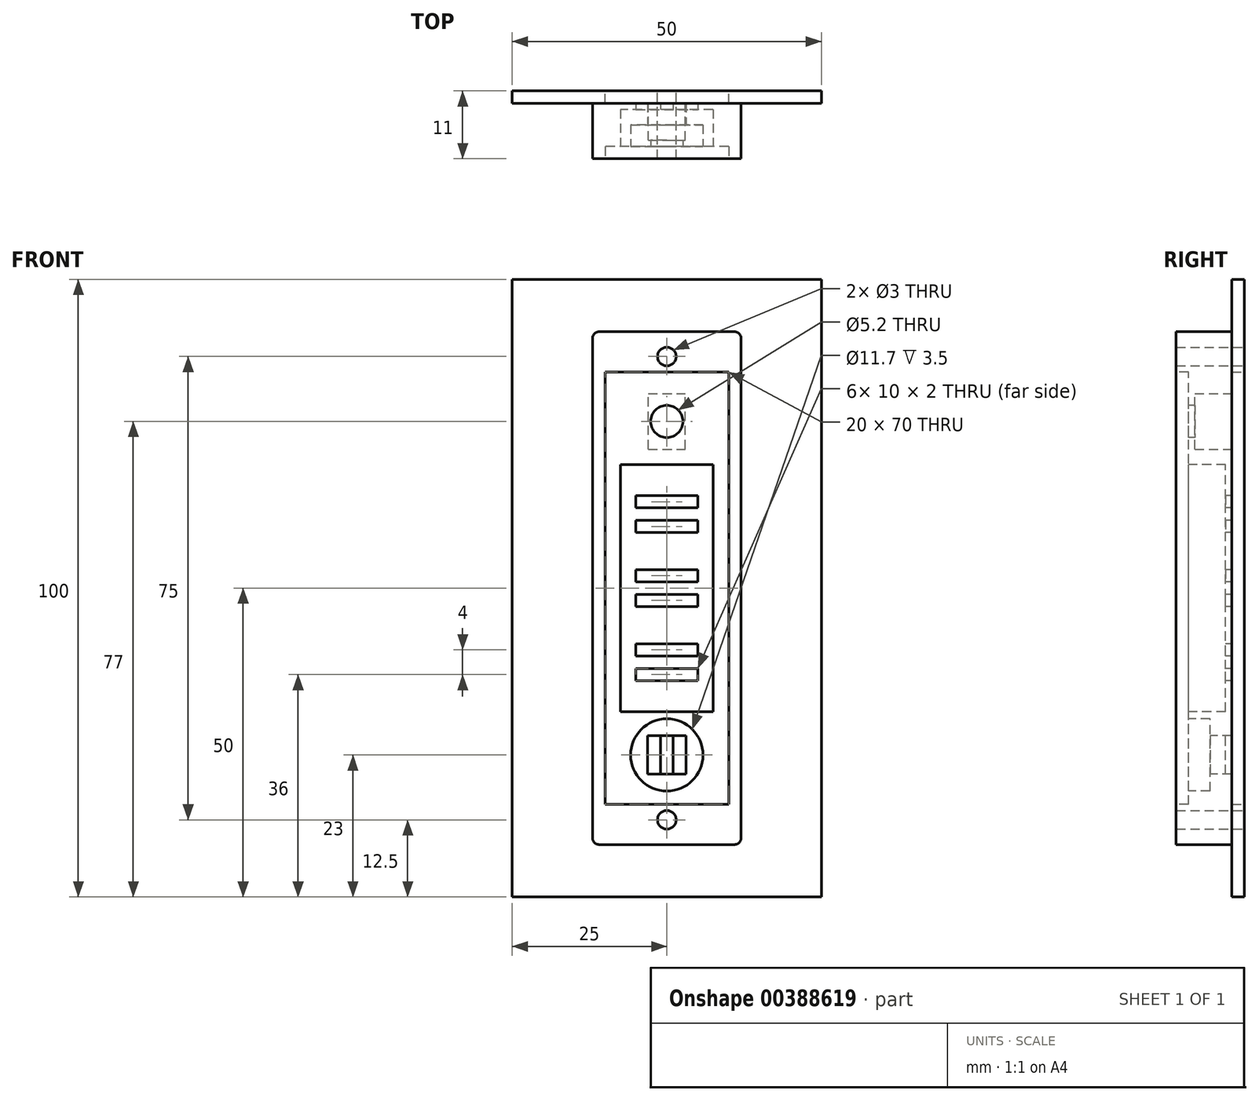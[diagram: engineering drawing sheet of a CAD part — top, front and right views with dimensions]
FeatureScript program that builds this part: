
annotation { "Feature Type Name" : "Feature", "Feature Type Description" : "" }
export const myFeature = defineFeature(function(context is Context, id is Id, definition is map)
    precondition{}
    {
        {
            var Q0;
            Q0=qCreatedBy(makeId("Front.planeOp"),FACE);
            var sketch = newSketch(context, id + "F0", { "sketchPlane" : qUnion([Q0])});
            skLineSegment(sketch, "E0.bottom", {"start": v(25, -50) * mm, "end": v(-25, -50) * mm});
            skLineSegment(sketch, "E0.top", {"start": v(25, 50) * mm, "end": v(-25, 50) * mm});
            skLineSegment(sketch, "E0.left", {"start": v(25, -50) * mm, "end": v(25, 50) * mm});
            skLineSegment(sketch, "E0.right", {"start": v(-25, -50) * mm, "end": v(-25, 50) * mm});
            skPoint(sketch, "E0.middle", {"position": v(0, 0) * mm});
            skLineSegment(sketch, "E1.bottom", {"start": v(10, -35) * mm, "end": v(-10, -35) * mm});
            skLineSegment(sketch, "E1.top", {"start": v(10, 35) * mm, "end": v(-10, 35) * mm});
            skLineSegment(sketch, "E1.left", {"start": v(10, -35) * mm, "end": v(10, 35) * mm});
            skLineSegment(sketch, "E1.right", {"start": v(-10, -35) * mm, "end": v(-10, 35) * mm});
            skCircle(sketch, "E2", {"center": v(0, 37.5) * mm, "radius": 1.5 * mm});
            skCircle(sketch, "E3", {"center": v(0, -37.5) * mm, "radius": 1.5 * mm});
            skSolve(sketch);
        }
        {
            var Q0;
            Q0 = qSketchRegion(id + "F0", true);
            extrude(context, id + "F1", {"entities" : qUnion([Q0]), "depth" : 2 * mm});
        }
        {
            var Q0;
            Q0=makeQuery(id+"F1.opExtrude","CAP_FACE",FACE,{"disambiguationData":[OSD([sQuery(id+"F0.wireOp",EDGE,"E0.bottom"),sQuery(id+"F0.wireOp",EDGE,"E0.top"),sQuery(id+"F0.wireOp",EDGE,"E0.left"),sQuery(id+"F0.wireOp",EDGE,"E0.right"),sQuery(id+"F0.wireOp",EDGE,"E1.bottom"),sQuery(id+"F0.wireOp",EDGE,"E1.top"),sQuery(id+"F0.wireOp",EDGE,"E1.left"),sQuery(id+"F0.wireOp",EDGE,"E1.right"),sQuery(id+"F0.wireOp",EDGE,"E2"),sQuery(id+"F0.wireOp",EDGE,"E3")])],"isStart":false});
            var sketch = newSketch(context, id + "F2", { "sketchPlane" : qUnion([Q0])});
            skLineSegment(sketch, "E4.bottom", {"start": v(12, -41.5) * mm, "end": v(-12, -41.5) * mm});
            skLineSegment(sketch, "E4.top", {"start": v(12, 41.5) * mm, "end": v(-12, 41.5) * mm});
            skLineSegment(sketch, "E4.left", {"start": v(12, -41.5) * mm, "end": v(12, 41.5) * mm});
            skLineSegment(sketch, "E4.right", {"start": v(-12, -41.5) * mm, "end": v(-12, 41.5) * mm});
            skPoint(sketch, "E4.middle", {"position": v(0, 0) * mm});
            skCircle(sketch, "E5", {"center": v(0, 37.5) * mm, "radius": 1.5 * mm});
            skCircle(sketch, "E6", {"center": v(0, -37.5) * mm, "radius": 1.5 * mm});
            skSolve(sketch);
        }
        {
            var Q0;
            Q0 = qSketchRegion(id + "F2", true);
            extrude(context, id + "F3", {"entities" : qUnion([Q0]), "depth" : 9 * mm});
        }
        {
            var Q0;
            Q0=makeQuery(id+"F3.opExtrude","CAP_FACE",FACE,{"disambiguationData":[OSD([sQuery(id+"F2.wireOp",EDGE,"E4.bottom"),sQuery(id+"F2.wireOp",EDGE,"E4.top"),sQuery(id+"F2.wireOp",EDGE,"E4.left"),sQuery(id+"F2.wireOp",EDGE,"E4.right")])],"isStart":false});
            var sketch = newSketch(context, id + "F4", { "sketchPlane" : qUnion([Q0])});
            skLineSegment(sketch, "E7.bottom", {"start": v(10, -35) * mm, "end": v(-10, -35) * mm});
            skLineSegment(sketch, "E7.top", {"start": v(10, 35) * mm, "end": v(-10, 35) * mm});
            skLineSegment(sketch, "E7.left", {"start": v(10, -35) * mm, "end": v(10, 35) * mm});
            skLineSegment(sketch, "E7.right", {"start": v(-10, -35) * mm, "end": v(-10, 35) * mm});
            skPoint(sketch, "E7.middle", {"position": v(0, 0) * mm});
            skSolve(sketch);
        }
        {
            var Q0;
            Q0 = qSketchRegion(id + "F4", true);
            extrude(context, id + "F5", {"entities" : qUnion([Q0]), "operationType" : NewBodyOperationType.REMOVE, "oppositeDirection" : true, "depth" : 14 * mm});
        }
        {
            var Q0;
            Q0=makeQuery(id+"F1.opExtrude","CAP_FACE",FACE,{"disambiguationData":[OSD([sQuery(id+"F0.wireOp",EDGE,"E0.bottom"),sQuery(id+"F0.wireOp",EDGE,"E0.top"),sQuery(id+"F0.wireOp",EDGE,"E0.left"),sQuery(id+"F0.wireOp",EDGE,"E0.right"),sQuery(id+"F0.wireOp",EDGE,"E1.bottom"),sQuery(id+"F0.wireOp",EDGE,"E1.top"),sQuery(id+"F0.wireOp",EDGE,"E1.left"),sQuery(id+"F0.wireOp",EDGE,"E1.right"),sQuery(id+"F0.wireOp",EDGE,"E2"),sQuery(id+"F0.wireOp",EDGE,"E3")])],"isStart":false});
            cPlane(context, id + "F6", {"entities" : qUnion([Q0]), "cplaneType" : CPlaneType.OFFSET, "offset" : 0 * mm, "width" : 150 * mm, "height" : 150 * mm});
        }
        {
            var Q0;
            Q0=qCreatedBy(id+"F6.planeOp",FACE);
            var sketch = newSketch(context, id + "F7", { "sketchPlane" : qUnion([Q0])});
            skLineSegment(sketch, "E8.bottom", {"start": v(10, -35) * mm, "end": v(-10, -35) * mm});
            skLineSegment(sketch, "E8.top", {"start": v(10, 35) * mm, "end": v(-10, 35) * mm});
            skLineSegment(sketch, "E8.left", {"start": v(10, -35) * mm, "end": v(10, 35) * mm});
            skLineSegment(sketch, "E8.right", {"start": v(-10, -35) * mm, "end": v(-10, 35) * mm});
            skPoint(sketch, "E8.middle", {"position": v(0, 0) * mm});
            skSolve(sketch);
        }
        {
            var Q0;
            Q0 = qSketchRegion(id + "F7", true);
            extrude(context, id + "F8", {"entities" : qUnion([Q0]), "operationType" : NewBodyOperationType.ADD, "depth" : 7 * mm});
        }
        {
            var Q0;
            Q0=makeQuery(id+"F8.opExtrude","CAP_FACE",FACE,{"disambiguationData":[OSD([sQuery(id+"F7.wireOp",EDGE,"E8.bottom"),sQuery(id+"F7.wireOp",EDGE,"E8.top"),sQuery(id+"F7.wireOp",EDGE,"E8.left"),sQuery(id+"F7.wireOp",EDGE,"E8.right")])],"isStart":false});
            var sketch = newSketch(context, id + "F9", { "sketchPlane" : qUnion([Q0])});
            skCircle(sketch, "E9", {"center": v(0, 27) * mm, "radius": 2.6 * mm});
            skLineSegment(sketch, "E10.bottom", {"start": v(2.5, 23) * mm, "end": v(-2.5, 23) * mm, "construction": true});
            skLineSegment(sketch, "E10.top", {"start": v(2.5, 31) * mm, "end": v(-2.5, 31) * mm, "construction": true});
            skLineSegment(sketch, "E10.left", {"start": v(2.5, 23) * mm, "end": v(2.5, 31) * mm, "construction": true});
            skLineSegment(sketch, "E10.right", {"start": v(-2.5, 23) * mm, "end": v(-2.5, 31) * mm, "construction": true});
            skCircle(sketch, "E11", {"center": v(-7.5, 32.5) * mm, "radius": 1 * mm, "construction": true});
            skCircle(sketch, "E12", {"center": v(7.5, 32.5) * mm, "radius": 1 * mm, "construction": true});
            skCircle(sketch, "E13", {"center": v(-7.5, -32.5) * mm, "radius": 1 * mm, "construction": true});
            skCircle(sketch, "E14", {"center": v(7.5, -32.5) * mm, "radius": 1 * mm, "construction": true});
            skSolve(sketch);
        }
        {
            var Q0;
            Q0 = qSketchRegion(id + "F9", true);
            extrude(context, id + "F10", {"entities" : qUnion([Q0]), "operationType" : NewBodyOperationType.REMOVE, "oppositeDirection" : true, "depth" : 5 * mm});
        }
        {
            var Q0;
            Q0=makeQuery(id+"F8.opExtrude","CAP_FACE",FACE,{"disambiguationData":[OSD([sQuery(id+"F7.wireOp",EDGE,"E8.bottom"),sQuery(id+"F7.wireOp",EDGE,"E8.top"),sQuery(id+"F7.wireOp",EDGE,"E8.left"),sQuery(id+"F7.wireOp",EDGE,"E8.right")])],"isStart":true});
            var sketch = newSketch(context, id + "F11", { "sketchPlane" : qUnion([Q0])});
            skLineSegment(sketch, "E15.bottom", {"start": v(3, 22.5) * mm, "end": v(-3, 22.5) * mm});
            skLineSegment(sketch, "E15.top", {"start": v(3, 31.5) * mm, "end": v(-3, 31.5) * mm});
            skLineSegment(sketch, "E15.left", {"start": v(3, 22.5) * mm, "end": v(3, 31.5) * mm});
            skLineSegment(sketch, "E15.right", {"start": v(-3, 22.5) * mm, "end": v(-3, 31.5) * mm});
            skPoint(sketch, "E15.middle", {"position": v(0, 27) * mm});
            skSolve(sketch);
        }
        {
            var Q0;
            Q0 = qSketchRegion(id + "F11", true);
            extrude(context, id + "F12", {"entities" : qUnion([Q0]), "operationType" : NewBodyOperationType.REMOVE, "oppositeDirection" : true, "depth" : 6 * mm});
        }
        {
            var Q0;
            Q0=makeQuery(id+"F8.opExtrude","CAP_FACE",FACE,{"disambiguationData":[OSD([sQuery(id+"F7.wireOp",EDGE,"E8.bottom"),sQuery(id+"F7.wireOp",EDGE,"E8.top"),sQuery(id+"F7.wireOp",EDGE,"E8.left"),sQuery(id+"F7.wireOp",EDGE,"E8.right")])],"isStart":false});
            var sketch = newSketch(context, id + "F13", { "sketchPlane" : qUnion([Q0])});
            skLineSegment(sketch, "E16.bottom", {"start": v(5, 13) * mm, "end": v(-5, 13) * mm});
            skLineSegment(sketch, "E16.top", {"start": v(5, 15) * mm, "end": v(-5, 15) * mm});
            skLineSegment(sketch, "E16.left", {"start": v(5, 13) * mm, "end": v(5, 15) * mm});
            skLineSegment(sketch, "E16.right", {"start": v(-5, 13) * mm, "end": v(-5, 15) * mm});
            skPoint(sketch, "E16.middle", {"position": v(0, 14) * mm});
            skLineSegment(sketch, "E17.bottom", {"start": v(5, 9) * mm, "end": v(-5, 9) * mm});
            skLineSegment(sketch, "E17.top", {"start": v(5, 11) * mm, "end": v(-5, 11) * mm});
            skLineSegment(sketch, "E17.left", {"start": v(5, 9) * mm, "end": v(5, 11) * mm});
            skLineSegment(sketch, "E17.right", {"start": v(-5, 9) * mm, "end": v(-5, 11) * mm});
            skPoint(sketch, "E17.middle", {"position": v(0, 10) * mm});
            skLineSegment(sketch, "E18.bottom", {"start": v(5, 1) * mm, "end": v(-5, 1) * mm});
            skLineSegment(sketch, "E18.top", {"start": v(5, 3) * mm, "end": v(-5, 3) * mm});
            skLineSegment(sketch, "E18.left", {"start": v(5, 1) * mm, "end": v(5, 3) * mm});
            skLineSegment(sketch, "E18.right", {"start": v(-5, 1) * mm, "end": v(-5, 3) * mm});
            skPoint(sketch, "E18.middle", {"position": v(0, 2) * mm});
            skLineSegment(sketch, "E19.bottom", {"start": v(5, -1) * mm, "end": v(-5, -1) * mm});
            skLineSegment(sketch, "E19.top", {"start": v(5, -3) * mm, "end": v(-5, -3) * mm});
            skLineSegment(sketch, "E19.left", {"start": v(5, -1) * mm, "end": v(5, -3) * mm});
            skLineSegment(sketch, "E19.right", {"start": v(-5, -1) * mm, "end": v(-5, -3) * mm});
            skPoint(sketch, "E19.middle", {"position": v(0, -2) * mm});
            skLineSegment(sketch, "E20.bottom", {"start": v(5, -9) * mm, "end": v(-5, -9) * mm});
            skLineSegment(sketch, "E20.top", {"start": v(5, -11) * mm, "end": v(-5, -11) * mm});
            skLineSegment(sketch, "E20.left", {"start": v(5, -9) * mm, "end": v(5, -11) * mm});
            skLineSegment(sketch, "E20.right", {"start": v(-5, -9) * mm, "end": v(-5, -11) * mm});
            skPoint(sketch, "E20.middle", {"position": v(0, -10) * mm});
            skPoint(sketch, "E20.middle.positionSnap0", {"position": v(0, -3) * mm});
            skPoint(sketch, "E20.centerSnap0", {"position": v(0, -3) * mm});
            skLineSegment(sketch, "E21.bottom", {"start": v(5, -13) * mm, "end": v(-5, -13) * mm});
            skLineSegment(sketch, "E21.top", {"start": v(5, -15) * mm, "end": v(-5, -15) * mm});
            skLineSegment(sketch, "E21.left", {"start": v(5, -13) * mm, "end": v(5, -15) * mm});
            skLineSegment(sketch, "E21.right", {"start": v(-5, -13) * mm, "end": v(-5, -15) * mm});
            skPoint(sketch, "E21.middle", {"position": v(0, -14) * mm});
            skSolve(sketch);
        }
        {
            var Q0;
            Q0 = qSketchRegion(id + "F13", true);
            extrude(context, id + "F14", {"entities" : qUnion([Q0]), "operationType" : NewBodyOperationType.REMOVE, "oppositeDirection" : true, "depth" : 10 * mm});
        }
        {
            var Q0;
            Q0=makeQuery(id+"F8.opExtrude","CAP_FACE",FACE,{"disambiguationData":[OSD([sQuery(id+"F7.wireOp",EDGE,"E8.bottom"),sQuery(id+"F7.wireOp",EDGE,"E8.top"),sQuery(id+"F7.wireOp",EDGE,"E8.left"),sQuery(id+"F7.wireOp",EDGE,"E8.right")])],"isStart":false});
            var sketch = newSketch(context, id + "F15", { "sketchPlane" : qUnion([Q0])});
            skLineSegment(sketch, "E22.bottom", {"start": v(7.5, -20) * mm, "end": v(-7.5, -20) * mm});
            skLineSegment(sketch, "E22.top", {"start": v(7.5, 20) * mm, "end": v(-7.5, 20) * mm});
            skLineSegment(sketch, "E22.left", {"start": v(7.5, -20) * mm, "end": v(7.5, 20) * mm});
            skLineSegment(sketch, "E22.right", {"start": v(-7.5, -20) * mm, "end": v(-7.5, 20) * mm});
            skPoint(sketch, "E22.middle", {"position": v(0, 0) * mm});
            skSolve(sketch);
        }
        {
            var Q0;
            Q0 = qSketchRegion(id + "F15", true);
            extrude(context, id + "F16", {"entities" : qUnion([Q0]), "operationType" : NewBodyOperationType.REMOVE, "oppositeDirection" : true, "depth" : 6 * mm});
        }
        {
            var Q0;
            Q0=makeQuery(id+"F8.opExtrude","CAP_FACE",FACE,{"disambiguationData":[OSD([sQuery(id+"F7.wireOp",EDGE,"E8.bottom"),sQuery(id+"F7.wireOp",EDGE,"E8.top"),sQuery(id+"F7.wireOp",EDGE,"E8.left"),sQuery(id+"F7.wireOp",EDGE,"E8.right")])],"isStart":false});
            var sketch = newSketch(context, id + "F17", { "sketchPlane" : qUnion([Q0])});
            skLineSegment(sketch, "E23.bottom", {"start": v(3.1, -30.1) * mm, "end": v(-3.1, -30.1) * mm});
            skLineSegment(sketch, "E23.top", {"start": v(3.1, -23.9) * mm, "end": v(-3.1, -23.9) * mm});
            skLineSegment(sketch, "E23.left", {"start": v(3.1, -30.1) * mm, "end": v(3.1, -23.9) * mm});
            skLineSegment(sketch, "E23.right", {"start": v(-3.1, -30.1) * mm, "end": v(-3.1, -23.9) * mm});
            skPoint(sketch, "E23.middle", {"position": v(0, -27) * mm});
            skSolve(sketch);
        }
        {
            var Q0;
            Q0 = qSketchRegion(id + "F17", true);
            extrude(context, id + "F18", {"entities" : qUnion([Q0]), "operationType" : NewBodyOperationType.REMOVE, "oppositeDirection" : true, "depth" : 6 * mm});
        }
        {
            var Q0;
            Q0=makeQuery(id+"F18.boolean.opBoolean","COPY",FACE,{"derivedFrom":makeQuery(id+"F18.opExtrude","CAP_FACE",FACE,{"disambiguationData":[OSD([sQuery(id+"F17.wireOp",EDGE,"E23.bottom"),sQuery(id+"F17.wireOp",EDGE,"E23.top"),sQuery(id+"F17.wireOp",EDGE,"E23.left"),sQuery(id+"F17.wireOp",EDGE,"E23.right")])],"isStart":false})});
            var sketch = newSketch(context, id + "F19", { "sketchPlane" : qUnion([Q0])});
            skLineSegment(sketch, "E24.bottom", {"start": v(-1, -30.1) * mm, "end": v(-3.1, -30.1) * mm});
            skLineSegment(sketch, "E24.top", {"start": v(-1, -23.9) * mm, "end": v(-3.1, -23.9) * mm});
            skLineSegment(sketch, "E24.left", {"start": v(-1, -30.1) * mm, "end": v(-1, -23.9) * mm});
            skLineSegment(sketch, "E24.right", {"start": v(-3.1, -30.1) * mm, "end": v(-3.1, -23.9) * mm});
            skPoint(sketch, "E24.middle", {"position": v(-2.05, -27) * mm});
            skPoint(sketch, "E24.middle.positionSnap0", {"position": v(3.1, -27) * mm});
            skPoint(sketch, "E24.centerSnap0", {"position": v(3.1, -27) * mm});
            skLineSegment(sketch, "E25.bottom", {"start": v(3.1, -30.1) * mm, "end": v(1, -30.1) * mm});
            skLineSegment(sketch, "E25.top", {"start": v(3.1, -23.9) * mm, "end": v(1, -23.9) * mm});
            skLineSegment(sketch, "E25.left", {"start": v(3.1, -30.1) * mm, "end": v(3.1, -23.9) * mm});
            skLineSegment(sketch, "E25.right", {"start": v(1, -30.1) * mm, "end": v(1, -23.9) * mm});
            skPoint(sketch, "E25.middle", {"position": v(2.05, -27) * mm});
            skSolve(sketch);
        }
        {
            var Q0;
            Q0 = qSketchRegion(id + "F19", true);
            extrude(context, id + "F20", {"entities" : qUnion([Q0]), "operationType" : NewBodyOperationType.REMOVE, "oppositeDirection" : true, "depth" : 1 * mm});
        }
        {
            var Q0;
            Q0=makeQuery(id+"F8.opExtrude","CAP_FACE",FACE,{"disambiguationData":[OSD([sQuery(id+"F7.wireOp",EDGE,"E8.bottom"),sQuery(id+"F7.wireOp",EDGE,"E8.top"),sQuery(id+"F7.wireOp",EDGE,"E8.left"),sQuery(id+"F7.wireOp",EDGE,"E8.right")])],"isStart":false});
            var sketch = newSketch(context, id + "F21", { "sketchPlane" : qUnion([Q0])});
            skCircle(sketch, "E26", {"center": v(0, -27) * mm, "radius": 5.85 * mm});
            skPoint(sketch, "E26.centerSnap0", {"position": v(3.1, -27) * mm});
            skPoint(sketch, "E26.centerSnap1", {"position": v(0, -23.9) * mm});
            skSolve(sketch);
        }
        {
            var Q0;
            Q0 = qSketchRegion(id + "F21", true);
            extrude(context, id + "F22", {"entities" : qUnion([Q0]), "operationType" : NewBodyOperationType.REMOVE, "oppositeDirection" : true, "depth" : 3.5 * mm});
        }
        {
            var Q0;
            Q0=makeQuery(id+"F3.opExtrude","SWEPT_EDGE",EDGE,{"disambiguationData":[OSD([sQuery(id+"F2.wireOp",EDGE,"E4.bottom"),sQuery(id+"F2.wireOp",EDGE,"E4.right")])]});
            var Q1;
            Q1=makeQuery(id+"F3.opExtrude","SWEPT_EDGE",EDGE,{"disambiguationData":[OSD([sQuery(id+"F2.wireOp",EDGE,"E4.bottom"),sQuery(id+"F2.wireOp",EDGE,"E4.left")])]});
            var Q2;
            Q2=makeQuery(id+"F3.opExtrude","SWEPT_EDGE",EDGE,{"disambiguationData":[OSD([sQuery(id+"F2.wireOp",EDGE,"E4.top"),sQuery(id+"F2.wireOp",EDGE,"E4.right")])]});
            var Q3;
            Q3=makeQuery(id+"F3.opExtrude","SWEPT_EDGE",EDGE,{"disambiguationData":[OSD([sQuery(id+"F2.wireOp",EDGE,"E4.top"),sQuery(id+"F2.wireOp",EDGE,"E4.left")])]});
            fillet(context, id + "F23", {"entities" : qUnion([Q0, Q1, Q2, Q3]), "radius" : 1 * mm, "tangentPropagation" : true, "allowEdgeOverflow" : false});
        }
    });
